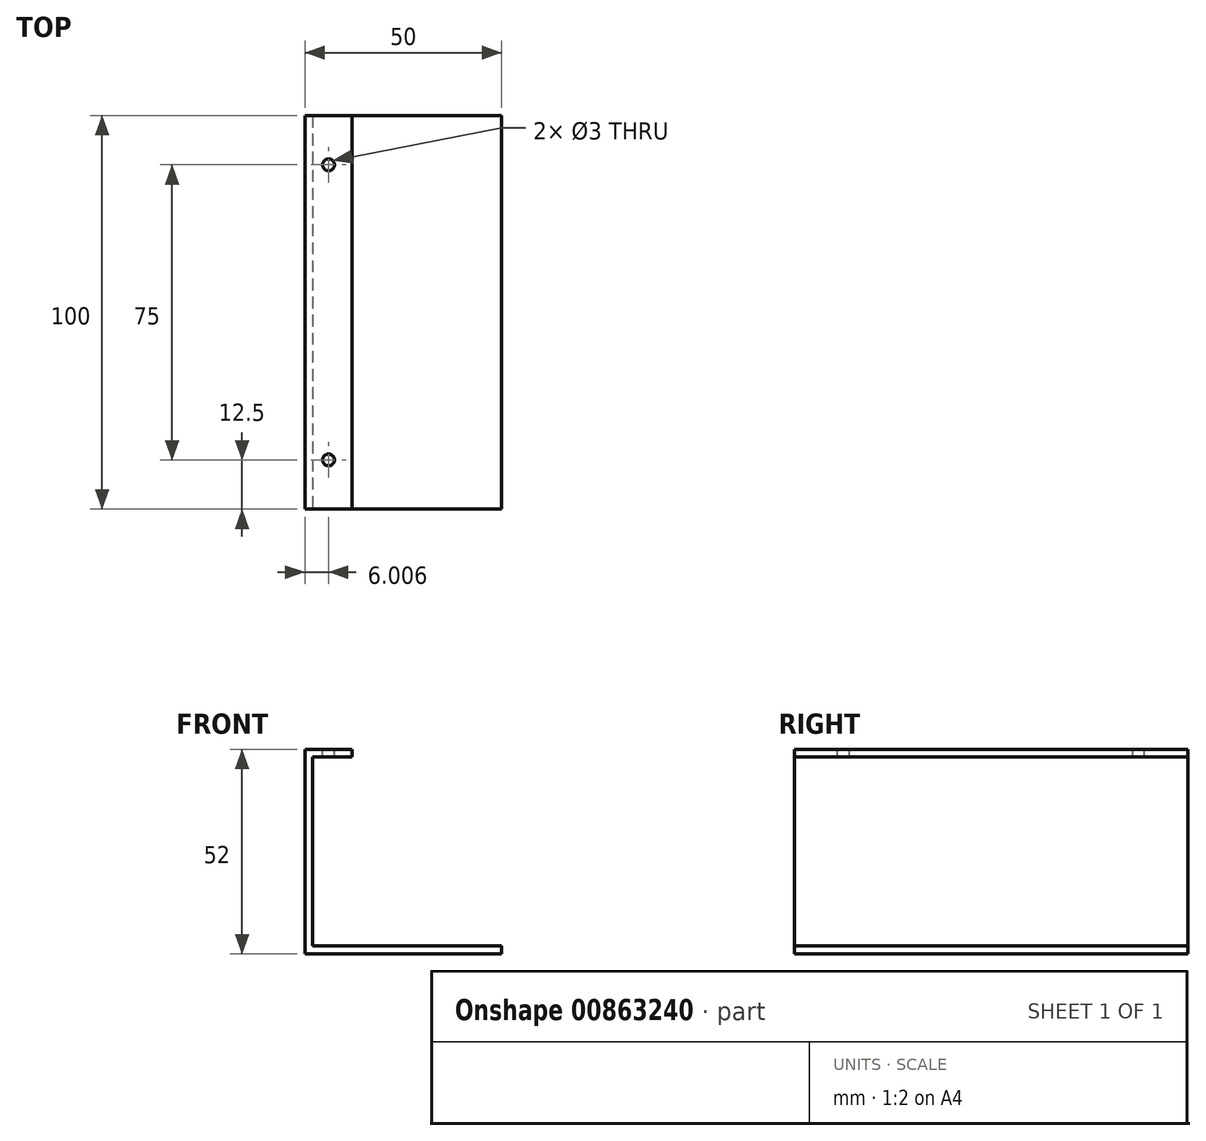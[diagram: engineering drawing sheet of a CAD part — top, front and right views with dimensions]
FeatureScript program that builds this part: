
annotation { "Feature Type Name" : "Feature", "Feature Type Description" : "" }
export const myFeature = defineFeature(function(context is Context, id is Id, definition is map)
    precondition{}
    {
        {
            var Q0;
            Q0=qCreatedBy(makeId("Top.planeOp"),FACE);
            var sketch = newSketch(context, id + "F0", { "sketchPlane" : qUnion([Q0])});
            skLineSegment(sketch, "E0.bottom", {"start": v(-25, 50) * mm, "end": v(25, 50) * mm});
            skLineSegment(sketch, "E0.top", {"start": v(-25, -50) * mm, "end": v(25, -50) * mm});
            skLineSegment(sketch, "E0.left", {"start": v(-25, 50) * mm, "end": v(-25, -50) * mm});
            skLineSegment(sketch, "E0.right", {"start": v(25, 50) * mm, "end": v(25, -50) * mm});
            skSolve(sketch);
        }
        {
            var Q0;
            Q0 = qSketchRegion(id + "F0", true);
            extrude(context, id + "F1", {"entities" : qUnion([Q0]), "depth" : 2 * mm, "offsetDistance" : 25.4 * mm});
        }
        {
            var Q0;
            Q0=makeQuery(id+"F1.opExtrude","CAP_FACE",FACE,{"disambiguationData":[OSD([sQuery(id+"F0.wireOp",EDGE,"E0.bottom"),sQuery(id+"F0.wireOp",EDGE,"E0.top"),sQuery(id+"F0.wireOp",EDGE,"E0.left"),sQuery(id+"F0.wireOp",EDGE,"E0.right")])],"isStart":false});
            var sketch = newSketch(context, id + "F2", { "sketchPlane" : qUnion([Q0])});
            skLineSegment(sketch, "E1.bottom", {"start": v(-25, 50) * mm, "end": v(-23, 50) * mm});
            skLineSegment(sketch, "E1.top", {"start": v(-25, -50) * mm, "end": v(-23, -50) * mm});
            skLineSegment(sketch, "E1.left", {"start": v(-25, 50) * mm, "end": v(-25, -50) * mm});
            skLineSegment(sketch, "E1.right", {"start": v(-23, 50) * mm, "end": v(-23, -50) * mm});
            skSolve(sketch);
        }
        {
            var Q0;
            Q0 = qSketchRegion(id + "F2", true);
            extrude(context, id + "F3", {"entities" : qUnion([Q0]), "operationType" : NewBodyOperationType.ADD, "depth" : 50 * mm, "offsetDistance" : 25.4 * mm});
        }
        {
            var Q0;
            Q0=makeQuery(id+"F3.opExtrude","SWEPT_FACE",FACE,{"disambiguationData":[OSD([sQuery(id+"F2.wireOp",EDGE,"E1.right")])]});
            var sketch = newSketch(context, id + "F4", { "sketchPlane" : qUnion([Q0])});
            skLineSegment(sketch, "E2.bottom", {"start": v(-50, 52) * mm, "end": v(50, 52) * mm});
            skLineSegment(sketch, "E2.top", {"start": v(-50, 50) * mm, "end": v(50, 50) * mm});
            skLineSegment(sketch, "E2.left", {"start": v(-50, 52) * mm, "end": v(-50, 50) * mm});
            skLineSegment(sketch, "E2.right", {"start": v(50, 52) * mm, "end": v(50, 50) * mm});
            skSolve(sketch);
        }
        {
            var Q0;
            Q0 = qSketchRegion(id + "F4", true);
            extrude(context, id + "F5", {"entities" : qUnion([Q0]), "operationType" : NewBodyOperationType.ADD, "depth" : 10 * mm, "offsetDistance" : 25.4 * mm});
        }
        {
            var Q0;
            Q0=makeQuery(id+"F5.boolean.opBoolean","MERGE",FACE,{"derivedFrom":[makeQuery(id+"F3.opExtrude","CAP_FACE",FACE,{"disambiguationData":[OSD([sQuery(id+"F2.wireOp",EDGE,"E1.bottom"),sQuery(id+"F2.wireOp",EDGE,"E1.top"),sQuery(id+"F2.wireOp",EDGE,"E1.left"),sQuery(id+"F2.wireOp",EDGE,"E1.right")])],"isStart":false}),makeQuery(id+"F5.opExtrude","SWEPT_FACE",FACE,{"disambiguationData":[OSD([sQuery(id+"F4.wireOp",EDGE,"E2.bottom")])]})]});
            var sketch = newSketch(context, id + "F6", { "sketchPlane" : qUnion([Q0])});
            skCircle(sketch, "E3", {"center": v(-19, 37.5) * mm, "radius": 1.5 * mm});
            skCircle(sketch, "E4", {"center": v(-19, -37.5) * mm, "radius": 1.5 * mm});
            skSolve(sketch);
        }
        {
            var Q0;
            Q0 = qSketchRegion(id + "F6", true);
            var Q1;
            Q1=makeQuery(id+"F5.opExtrude","SWEPT_FACE",FACE,{"disambiguationData":[OSD([sQuery(id+"F4.wireOp",EDGE,"E2.top")])]});
            extrude(context, id + "F7", {"entities" : qUnion([Q0]), "operationType" : NewBodyOperationType.REMOVE, "endBound" : BoundingType.UP_TO_SURFACE, "oppositeDirection" : true, "depth" : 25.4 * mm, "endBoundEntityFace" : qUnion([Q1]), "offsetDistance" : 25.4 * mm});
        }
    });
